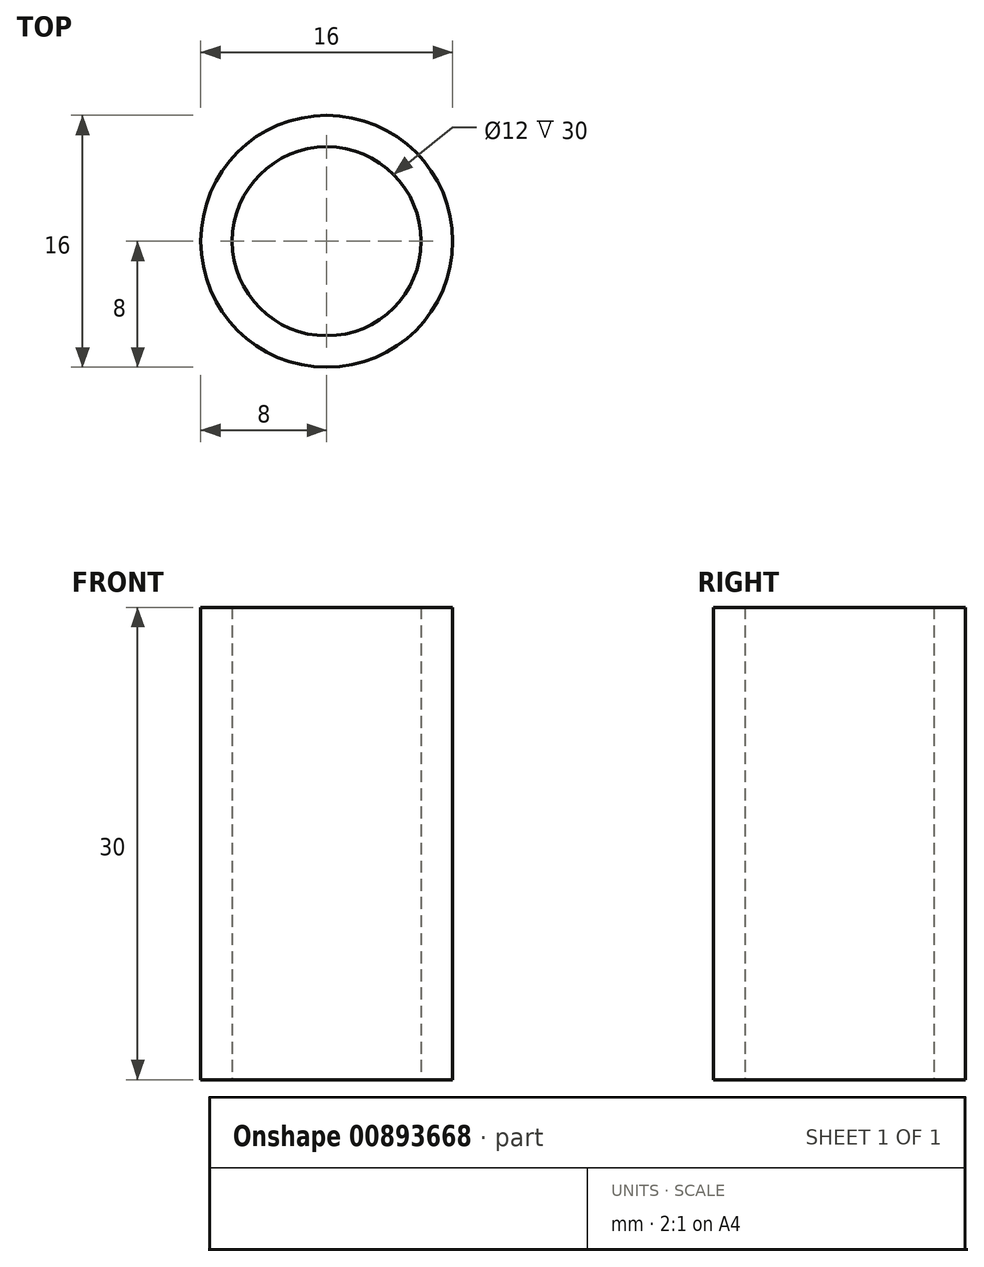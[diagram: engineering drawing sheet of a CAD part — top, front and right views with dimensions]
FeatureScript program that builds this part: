
annotation { "Feature Type Name" : "Feature", "Feature Type Description" : "" }
export const myFeature = defineFeature(function(context is Context, id is Id, definition is map)
    precondition{}
    {
        {
            var Q0;
            Q0=qCreatedBy(makeId("Top.planeOp"),FACE);
            var sketch = newSketch(context, id + "F0", { "sketchPlane" : qUnion([Q0])});
            skCircle(sketch, "E0", {"center": v(0, 0) * mm, "radius": 8 * mm});
            skCircle(sketch, "E1", {"center": v(0, 0) * mm, "radius": 6 * mm});
            skSolve(sketch);
        }
        {
            var Q0;
            Q0 = qSketchRegion(id + "F0", true);
            extrude(context, id + "F1", {"entities" : qUnion([Q0]), "depth" : 30 * mm, "offsetDistance" : 25 * mm});
        }
    });
